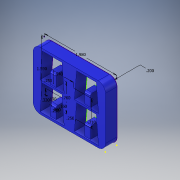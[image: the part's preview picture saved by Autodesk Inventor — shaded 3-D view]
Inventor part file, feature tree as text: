
AUTODESK INVENTOR PART (.ipt)
format: ipt  version: 2018 (Build 220112000, 112)  size: 250,368 bytes
history: native  units: in
note: dims shown in document units (in); Inventor stores cm internally (conversion verified against a paired STEP export)
features: sketch x3, extrude x2, fillet x1, shell x1, projected_geometry x1
ambient origin geometry x8: Origin, YZ Plane, XZ Plane, XY Plane, X Axis, Y Axis, Z Axis, Center Point
bodies: Solid1 (feature_tree)
feature tree (8):
  sketch  "Sketch1"  dims[d0=1.98in d1=1.59in]
  extrude  "Extrusion1"  Depth=1.59in
  sketch  "Sketch2"  dims[d2=0.19in d3=0.25in d4=0.25in d6=0.54in]
  extrude  "Extrusion2"  Depth=0.19in
  fillet  "Fillet1"  Radius=0.25in
  shell  "Shell1"  Thickness=0.54in
  sketch  "Sketch3"  dims[d7=0.25in d8=0.06in d10=0.32in d12=0.16in d13=0.71in d14=0.7874in d16=0.76in d17=0.3937in d19=1.0in d21=0.2in d22=0.31in d23=0.0in d24=0.03in d25=0.0in d26=0.05in d27=0.01in]
  projected_geometry  "Projected Loop1"
